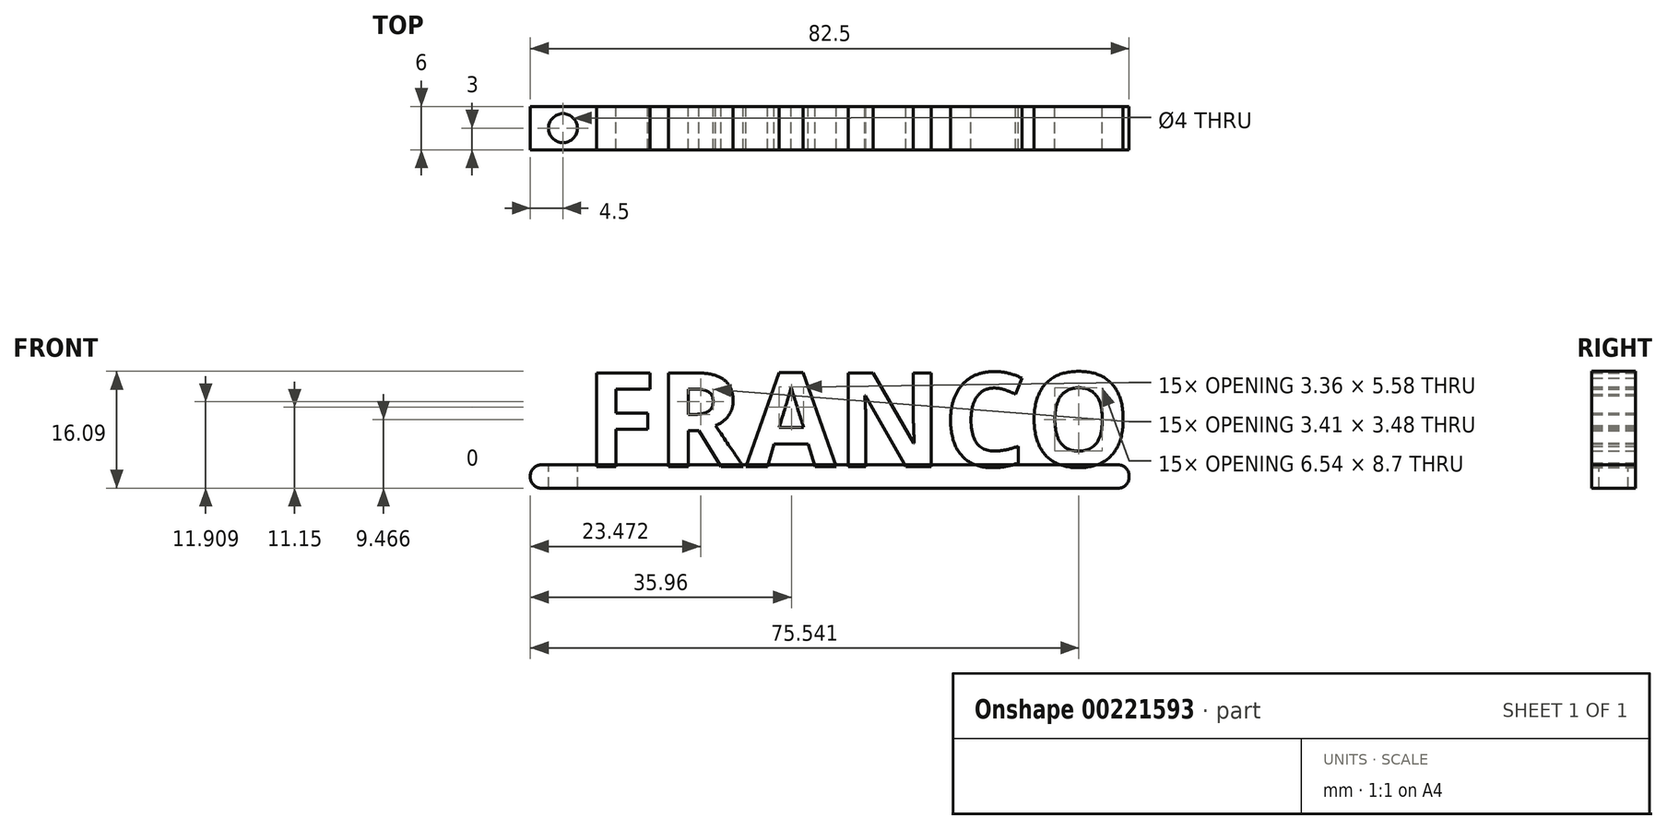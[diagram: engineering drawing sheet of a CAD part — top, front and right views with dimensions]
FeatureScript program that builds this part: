
annotation { "Feature Type Name" : "Feature", "Feature Type Description" : "" }
export const myFeature = defineFeature(function(context is Context, id is Id, definition is map)
    precondition{}
    {
        {
            var Q0;
            Q0=qCreatedBy(makeId("Front.planeOp"),FACE);
            var sketch = newSketch(context, id + "F0", { "sketchPlane" : qUnion([Q0])});
            skText(sketch, "E0", { "text": "FRANCO", "fontName": "OpenSans-Bold.ttf"});
            const initialGuessF0  = {"E0": [-0.02, 0, 1, 0, 0.013]};
            skSetInitialGuess(sketch, initialGuessF0);
            skSolve(sketch);
        }
        {
            var Q0;
            Q0=qSketchRegion(id+"F0",true);
            extrude(context, id + "F1", {"entities" : qUnion([Q0]), "endBound" : BoundingType.SYMMETRIC, "depth" : 6 * mm});
        }
        {
            var Q0;
            Q0=qCreatedBy(makeId("Top.planeOp"),FACE);
            var sketch = newSketch(context, id + "F2", { "sketchPlane" : qUnion([Q0])});
            skLineSegment(sketch, "E1.bottom", {"start": v(-20, 3) * mm, "end": v(55, 3) * mm});
            skLineSegment(sketch, "E1.top", {"start": v(-20, -3) * mm, "end": v(55, -3) * mm});
            skLineSegment(sketch, "E1.left", {"start": v(-20, 3) * mm, "end": v(-20, -3) * mm});
            skLineSegment(sketch, "E1.right", {"start": v(55, 3) * mm, "end": v(55, -3) * mm});
            skSolve(sketch);
        }
        {
            var Q0;
            Q0=makeQuery(id+"F2.imprint","IMPRINT",FACE,{"disambiguationData":[TD([[makeQuery(id+"F2.imprint","IMPRINT",EDGE,{"derivedFrom":sQuery(id+"F2.wireOp",EDGE,"E1.bottom")}),-1.0]])]});
            extrude(context, id + "F3", {"entities" : qUnion([Q0]), "depth" : 0.2 * mm});
        }
        {
            var Q0;
            Q0=makeQuery(id+"F3.opExtrude","CAP_FACE",FACE,{"disambiguationData":[OSD([sQuery(id+"F2.wireOp",EDGE,"E1.bottom"),sQuery(id+"F2.wireOp",EDGE,"E1.top"),sQuery(id+"F2.wireOp",EDGE,"E1.left"),sQuery(id+"F2.wireOp",EDGE,"E1.right")])],"isStart":true});
            extrude(context, id + "F4", {"entities" : qUnion([Q0]), "depth" : 3 * mm});
        }
        {
            var Q0;
            {var subQ0=sQuery(id+"F2.wireOp",EDGE,"E1.left");Q0=makeQuery(id+"FaVoHrOpcFZXiYX_6.opBoolean","MERGE",FACE,{"derivedFrom":[makeQuery(id+"F3.opExtrude","SWEPT_FACE",FACE,{"disambiguationData":[OSD([subQ0])]}),makeQuery(id+"F4.opExtrude","SWEPT_FACE",FACE,{"disambiguationData":[OSD([subQ0])]})]});}
            var sketch = newSketch(context, id + "F5", { "sketchPlane" : qUnion([Q0])});
            skLineSegment(sketch, "E2.bottom", {"start": v(-3, -3) * mm, "end": v(3, -3) * mm});
            skLineSegment(sketch, "E2.top", {"start": v(-3, 0.2) * mm, "end": v(3, 0.2) * mm});
            skLineSegment(sketch, "E2.left", {"start": v(-3, -3) * mm, "end": v(-3, 0.2) * mm});
            skLineSegment(sketch, "E2.right", {"start": v(3, -3) * mm, "end": v(3, 0.2) * mm});
            skSolve(sketch);
        }
        {
            var Q0;
            Q0=qSketchRegion(id+"F5",true);
            extrude(context, id + "F6", {"entities" : qUnion([Q0]), "operationType" : NewBodyOperationType.ADD, "depth" : 7.5 * mm});
        }
        {
            var Q0;
            Q0=makeQuery(id+"F6.opExtrude","CAP_EDGE",EDGE,{"disambiguationData":[OSD([sQuery(id+"F5.wireOp",EDGE,"E2.bottom")])],"isStart":false});
            var Q1;
            Q1=makeQuery(id+"F6.opExtrude","CAP_EDGE",EDGE,{"disambiguationData":[OSD([sQuery(id+"F5.wireOp",EDGE,"E2.top")])],"isStart":false});
            var Q2;
            Q2=makeQuery(id+"F4.opExtrude","CAP_EDGE",EDGE,{"disambiguationData":[OSD([sQuery(id+"F2.wireOp",EDGE,"E1.right")])],"isStart":false});
            fillet(context, id + "F7", {"entities" : qUnion([Q0, Q1, Q2]), "radius" : 1.5 * mm, "tangentPropagation" : true, "allowEdgeOverflow" : false});
        }
        {
            var Q0;
            {var subQ19=sQuery(id+"F2.wireOp",EDGE,"E1.top");var subQ20=sQuery(id+"F2.wireOp",EDGE,"E1.bottom");var subQ63=sQuery(id+"F0.wireOp",EDGE,"E0.sketch_text.stroke-2");var subQ66=sQuery(id+"F2.wireOp",EDGE,"E1.left");Q0=makeQuery(id+"F6.boolean.opBoolean","MERGE",FACE,{"derivedFrom":[makeQuery(id+"FaVoHrOpcFZXiYX_6.opBoolean","SPLIT",FACE,{"disambiguationData":[TD([makeQuery(id+"F1.opExtrude","SWEPT_FACE",FACE,{"disambiguationData":[OSD([subQ63])]})])],"derivedFrom":makeQuery(id+"F3.opExtrude","CAP_FACE",FACE,{"disambiguationData":[OSD([subQ20,subQ19,subQ66,sQuery(id+"F2.wireOp",EDGE,"E1.right")])],"isStart":false})}),makeQuery(id+"F6.opExtrude","SWEPT_FACE",FACE,{"disambiguationData":[OSD([sQuery(id+"F5.wireOp",EDGE,"E2.top")])]})]});}
            var sketch = newSketch(context, id + "F8", { "sketchPlane" : qUnion([Q0])});
            skCircle(sketch, "E3", {"center": v(-23, 0) * mm, "radius": 2 * mm});
            skSolve(sketch);
        }
        {
            var Q0;
            Q0=makeQuery(id+"F8.imprint","IMPRINT",FACE,{"disambiguationData":[TD([[makeQuery(id+"F8.imprint","IMPRINT",EDGE,{"derivedFrom":sQuery(id+"F8.wireOp",EDGE,"E3")}),1.0]])]});
            extrude(context, id + "F9", {"entities" : qUnion([Q0]), "operationType" : NewBodyOperationType.REMOVE, "oppositeDirection" : true, "depth" : 3.5 * mm});
        }
        {
            var Q0;
            Q0=makeQuery(id+"F3.opExtrude","CAP_EDGE",EDGE,{"disambiguationData":[OSD([sQuery(id+"F2.wireOp",EDGE,"E1.right")])],"isStart":false});
            fillet(context, id + "F10", {"entities" : qUnion([Q0]), "radius" : 1.5 * mm, "tangentPropagation" : true, "allowEdgeOverflow" : false});
        }
    });
